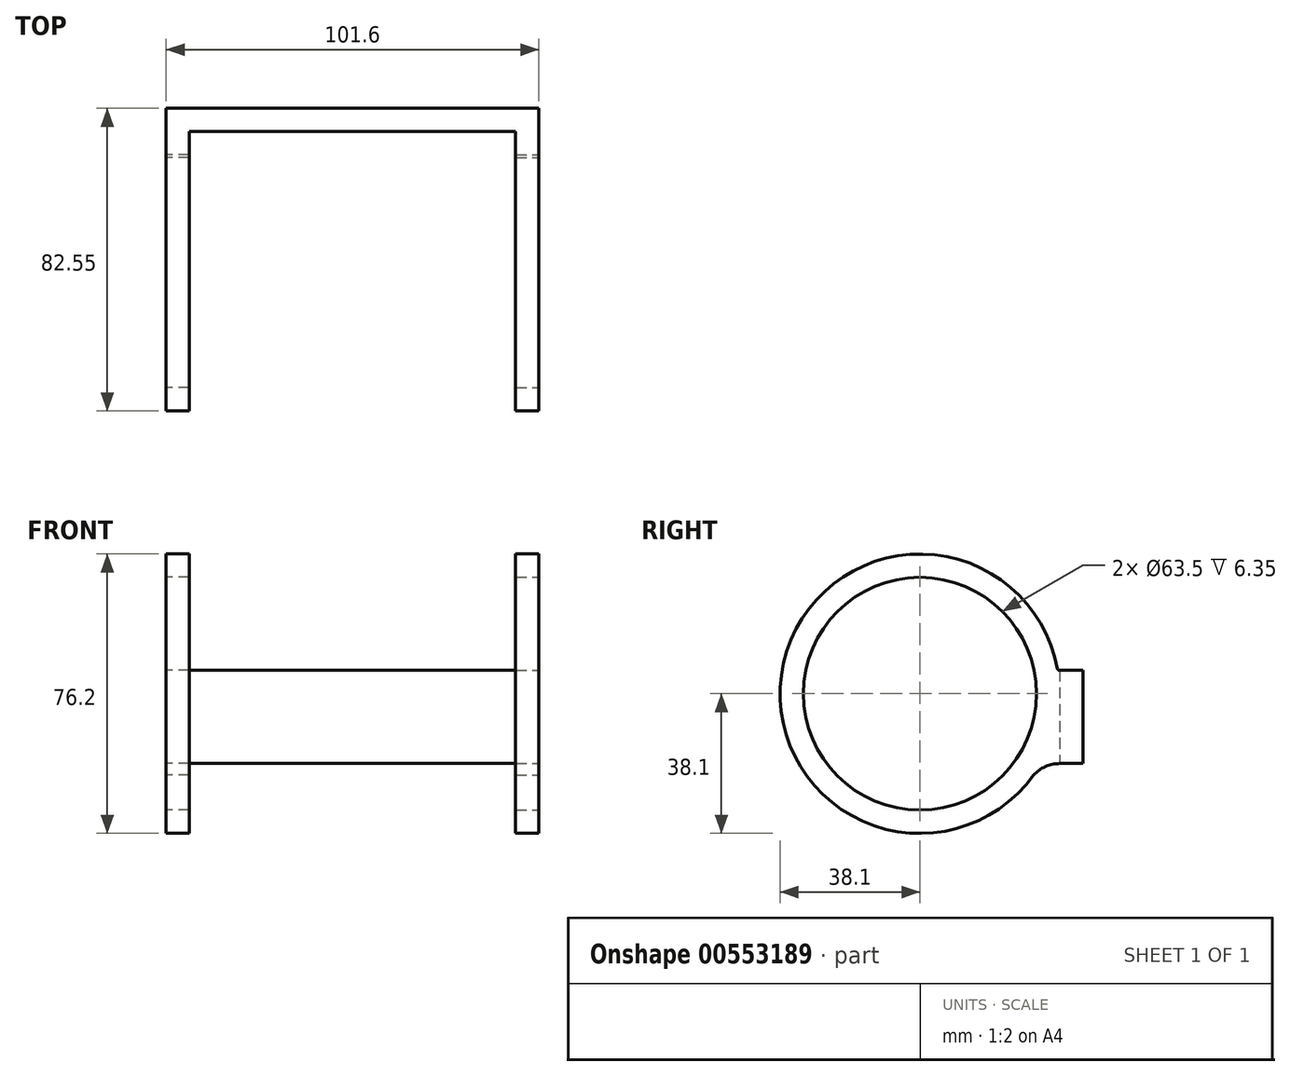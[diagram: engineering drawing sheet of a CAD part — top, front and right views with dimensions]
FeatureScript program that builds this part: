
annotation { "Feature Type Name" : "Feature", "Feature Type Description" : "" }
export const myFeature = defineFeature(function(context is Context, id is Id, definition is map)
    precondition{}
    {
        {
            var Q0;
            Q0=qCreatedBy(makeId("Right.planeOp"),FACE);
            var sketch = newSketch(context, id + "F0", { "sketchPlane" : qUnion([Q0])});
            skCircle(sketch, "E0", {"center": v(0, 0) * mm, "radius": 31.75 * mm});
            skArc(sketch, "E1", {"start": v(27.4, 26.48) * mm, "mid": v(-37.58, 6.27) * mm, "end": v(17.32, -33.94) * mm});
            skCircle(sketch, "E2", {"center": v(0, 0) * mm, "radius": 38.1 * mm});
            skLineSegment(sketch, "E3", {"start": v(38.1, -19.05) * mm, "end": v(44.45, -19.05) * mm});
            skLineSegment(sketch, "E4", {"start": v(44.45, -19.05) * mm, "end": v(44.45, 6.35) * mm});
            skLineSegment(sketch, "E5", {"start": v(44.45, 6.35) * mm, "end": v(38.08, 6.35) * mm});
            skArc(sketch, "E6", {"start": v(38.1, -19.05) * mm, "mid": v(34.21, -19.87) * mm, "end": v(30.98, -22.17) * mm});
            skPoint(sketch, "E7.start.orphan", {"position": v(38.1, 0) * mm});
            skArc(sketch, "E8", {"start": v(37.48, 6.85) * mm, "mid": v(37.7, 6.5) * mm, "end": v(38.08, 6.35) * mm});
            skSolve(sketch);
        }
        {
            var Q0;
            Q0=makeQuery(id+"F0.imprint","IMPRINT",FACE,{"disambiguationData":[TD([[makeQuery(id+"F0.imprint","IMPRINT",EDGE,{"derivedFrom":sQuery(id+"F0.wireOp",EDGE,"E0")}),-1.0]])]});
            var Q1;
            Q1=makeQuery(id+"F0.imprint","IMPRINT",FACE,{"disambiguationData":[TD([[makeQuery(id+"F0.imprint","IMPRINT",EDGE,{"derivedFrom":sQuery(id+"F0.wireOp",EDGE,"E3")}),1.0]])]});
            extrude(context, id + "F1", {"entities" : qUnion([Q0, Q1]), "depth" : 6.35 * mm, "offsetDistance" : 25.4 * mm});
        }
        {
            var Q0;
            Q0=makeQuery(id+"F1.opExtrude","CAP_FACE",FACE,{"disambiguationData":[OSD([sQuery(id+"F0.wireOp",EDGE,"E0"),sQuery(id+"F0.wireOp",EDGE,"E2"),sQuery(id+"F0.wireOp",EDGE,"E3"),sQuery(id+"F0.wireOp",EDGE,"E4"),sQuery(id+"F0.wireOp",EDGE,"E5"),sQuery(id+"F0.wireOp",EDGE,"E6"),sQuery(id+"F0.wireOp",EDGE,"E8")])],"isStart":false});
            var sketch = newSketch(context, id + "F2", { "sketchPlane" : qUnion([Q0])});
            skLineSegment(sketch, "E9.bottom", {"start": v(44.45, 6.35) * mm, "end": v(38.1, 6.35) * mm});
            skLineSegment(sketch, "E9.top", {"start": v(44.45, -19.05) * mm, "end": v(38.1, -19.05) * mm});
            skLineSegment(sketch, "E9.left", {"start": v(44.45, 6.35) * mm, "end": v(44.45, -19.05) * mm});
            skLineSegment(sketch, "E9.right", {"start": v(38.1, 6.35) * mm, "end": v(38.1, -19.05) * mm});
            skSolve(sketch);
        }
        {
            var Q0;
            Q0=makeQuery(id+"F2.imprint","IMPRINT",FACE,{"disambiguationData":[TD([[makeQuery(id+"F2.imprint","IMPRINT",EDGE,{"derivedFrom":sQuery(id+"F2.wireOp",EDGE,"E9.bottom")}),1.0]])]});
            extrude(context, id + "F3", {"entities" : qUnion([Q0]), "operationType" : NewBodyOperationType.ADD, "depth" : 44.45 * mm, "offsetDistance" : 25.4 * mm});
        }
        {
            var Q0;
            Q0=makeQuery(id+"F1.opExtrude","SWEPT_BODY",BODY,{"disambiguationData":[OSD([sQuery(id+"F0.wireOp",EDGE,"E0"),sQuery(id+"F0.wireOp",EDGE,"FDSLf29t-neqX-oQhH-1RVA-G03Dy36ElSPa"),sQuery(id+"F0.wireOp",EDGE,"cmFVJZx4-tZeq-SRAW-oc0z-0U0u9Pgw5cSu"),sQuery(id+"F0.wireOp",EDGE,"E1"),sQuery(id+"F0.wireOp",EDGE,"dxBUt8oM-uTJt-TWNZ-GT2I-5leSRlBEpvTV"),sQuery(id+"F0.wireOp",EDGE,"cH5itxg4-RyMf-NnTr-wv4z-vrQa4O4trerF")])]});
            var Q1;
            Q1=makeQuery(id+"F3.opExtrude","CAP_FACE",FACE,{"disambiguationData":[OSD([sQuery(id+"F2.wireOp",EDGE,"E9.bottom"),sQuery(id+"F2.wireOp",EDGE,"E9.top"),sQuery(id+"F2.wireOp",EDGE,"E9.left"),sQuery(id+"F2.wireOp",EDGE,"E9.right")])],"isStart":false});
            mirror(context, id + "F4", {"operationType" : NewBodyOperationType.ADD, "entities" : qUnion([Q0]), "mirrorPlane" : qUnion([Q1])});
        }
    });
